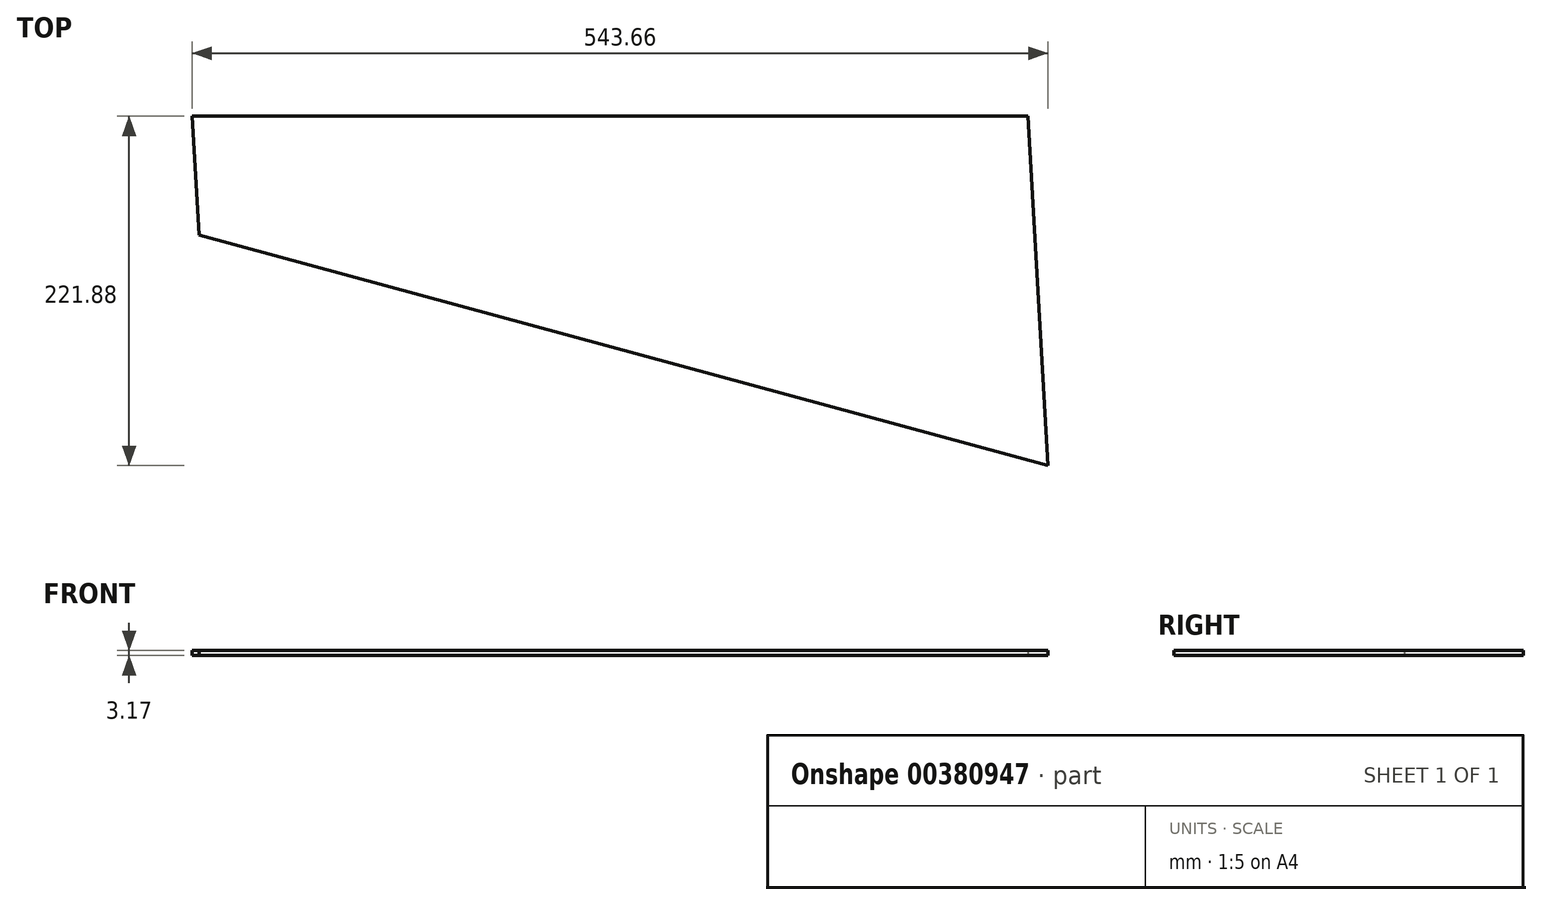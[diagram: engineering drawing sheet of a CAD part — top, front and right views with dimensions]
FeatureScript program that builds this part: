
annotation { "Feature Type Name" : "Feature", "Feature Type Description" : "" }
export const myFeature = defineFeature(function(context is Context, id is Id, definition is map)
    precondition{}
    {
        {
            var Q0;
            Q0=qCreatedBy(makeId("Top.planeOp"),FACE);
            var sketch = newSketch(context, id + "F0", { "sketchPlane" : qUnion([Q0])});
            skLineSegment(sketch, "E0", {"start": v(0, 0) * mm, "end": v(12.85, -221.88) * mm});
            skLineSegment(sketch, "E1", {"start": v(12.85, -221.88) * mm, "end": v(-526.44, -75.51) * mm});
            skLineSegment(sketch, "E2", {"start": v(-526.44, -75.51) * mm, "end": v(-530.81, 0) * mm});
            skLineSegment(sketch, "E3", {"start": v(-530.81, 0) * mm, "end": v(0, 0) * mm});
            skSolve(sketch);
        }
        {
            var Q0;
            Q0=qSketchRegion(id+"F0",true);
            extrude(context, id + "F1", {"entities" : qUnion([Q0]), "depth" : 3.17 * mm});
        }
    });
